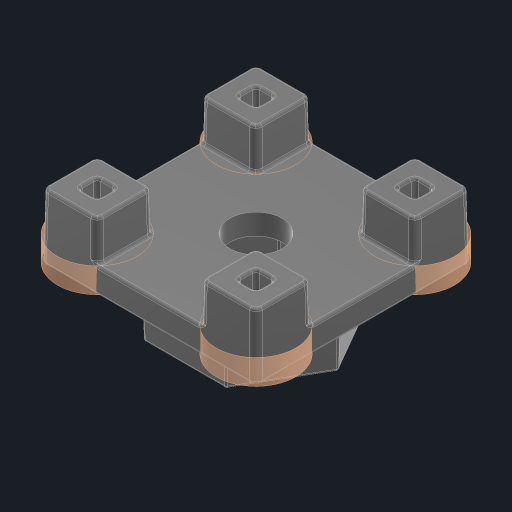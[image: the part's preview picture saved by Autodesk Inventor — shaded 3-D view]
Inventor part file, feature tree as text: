
AUTODESK INVENTOR PART (.ipt)
format: ipt  version: 2023 (Build 270158030, 158C)  size: 693,760 bytes
history: native  units: in
note: dims shown in document units (in); Inventor stores cm internally (conversion verified against a paired STEP export)
features: extrude x5, projected_geometry x4, other x4, sketch x3, pattern_linear x1, fillet x1
ambient origin geometry x8: Origin, YZ Plane, XZ Plane, XY Plane, X Axis, Y Axis, Z Axis, Center Point
bodies: Solid1 (feature_tree)
feature tree (18):
  sketch  "Sketch2"  dims[d1=0.25in]
  pattern_linear  "Rectangular Pattern1"  Spacing1=0.25in  [1 undecoded]
  extrude  "Extrusion1"  Depth=0.0787in TaperAngle=0.0deg
  sketch  "Sketch1"  dims[d0=0.25in]
  projected_geometry  "Projected Loop1"
  projected_geometry  "Projected Loop2"
  projected_geometry  "Projected Loop3"
  projected_geometry  "Projected Loop4"
  other  "Srf1"
  other  "Srf5"
  other  "Srf6"
  other  "Srf7"
  sketch  "Sketch5"  dims[d2=0.25in d3=0.25in d4=0.0787in d5=0.0in d6=0.25in d7=0.25in d8=0.25in d9=0.25in d24=0.7874in d26=0.5in d27=0.7874in d29=0.5in d30=0.25in d31=0.25in d32=1.0in d33=0.0in]
  fillet  "Fillet8"  Radius=0.25in
  extrude  "ExtrusionSrf1"  Depth=0.7874in
  extrude  "ExtrusionSrf5"  Depth=0.7874in
  extrude  "ExtrusionSrf6"  Depth=0.25in
  extrude  "ExtrusionSrf7"  Depth=0.25in
note: 1 required parameter value undecoded (feature->parameter linkage not recoverable at this tier; creation-order binding heuristic only, values carry confidence <= 0.55)
